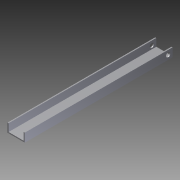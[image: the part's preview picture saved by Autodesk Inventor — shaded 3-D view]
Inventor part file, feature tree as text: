
AUTODESK INVENTOR PART (.ipt)
format: ipt  version: 2012 (Build 160160000, 160)  size: 87,552 bytes
history: native  units: in
note: dims shown in document units (in); Inventor stores cm internally (conversion verified against a paired STEP export)
features: extrude x2, sketch x2
ambient origin geometry x8: Origin, YZ Plane, XZ Plane, XY Plane, X Axis, Y Axis, Z Axis, Center Point
bodies: Solid1 (feature_tree)
feature tree (4):
  extrude  "Extrusion1"  Depth=1.0in
  extrude  "Extrusion2"  Depth=0.125in
  sketch  "Sketch1"  dims[d0=2.0in d1=1.0in]
  sketch  "Sketch2"  dims[d2=0.125in d3=0.125in d4=0.125in d5=0.125in d6=17.0in d7=0.0in d8=0.5in d9=0.5in d10=0.5in d11=17.0in d12=0.0in]
